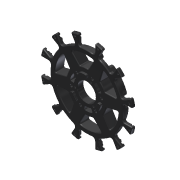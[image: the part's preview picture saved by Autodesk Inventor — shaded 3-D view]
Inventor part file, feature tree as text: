
AUTODESK INVENTOR PART (.ipt)
format: ipt  version: 2013 (Build 170138000, 138)  size: 1,256,448 bytes
history: native  units: in
note: dims shown in document units (in); Inventor stores cm internally (conversion verified against a paired STEP export)
features: chamfer x1, other x1, imported_body x1
ambient origin geometry x8: Origin, YZ Plane, XZ Plane, XY Plane, X Axis, Y Axis, Z Axis, Center Point
feature tree (3):
  chamfer  "Chamfer1"  [1 undecoded]
  other  "Omni Wheel Hub 6 inch"
  imported_body  "Base1"
note: 1 required parameter value undecoded (feature->parameter linkage not recoverable at this tier; creation-order binding heuristic only, values carry confidence <= 0.55)
